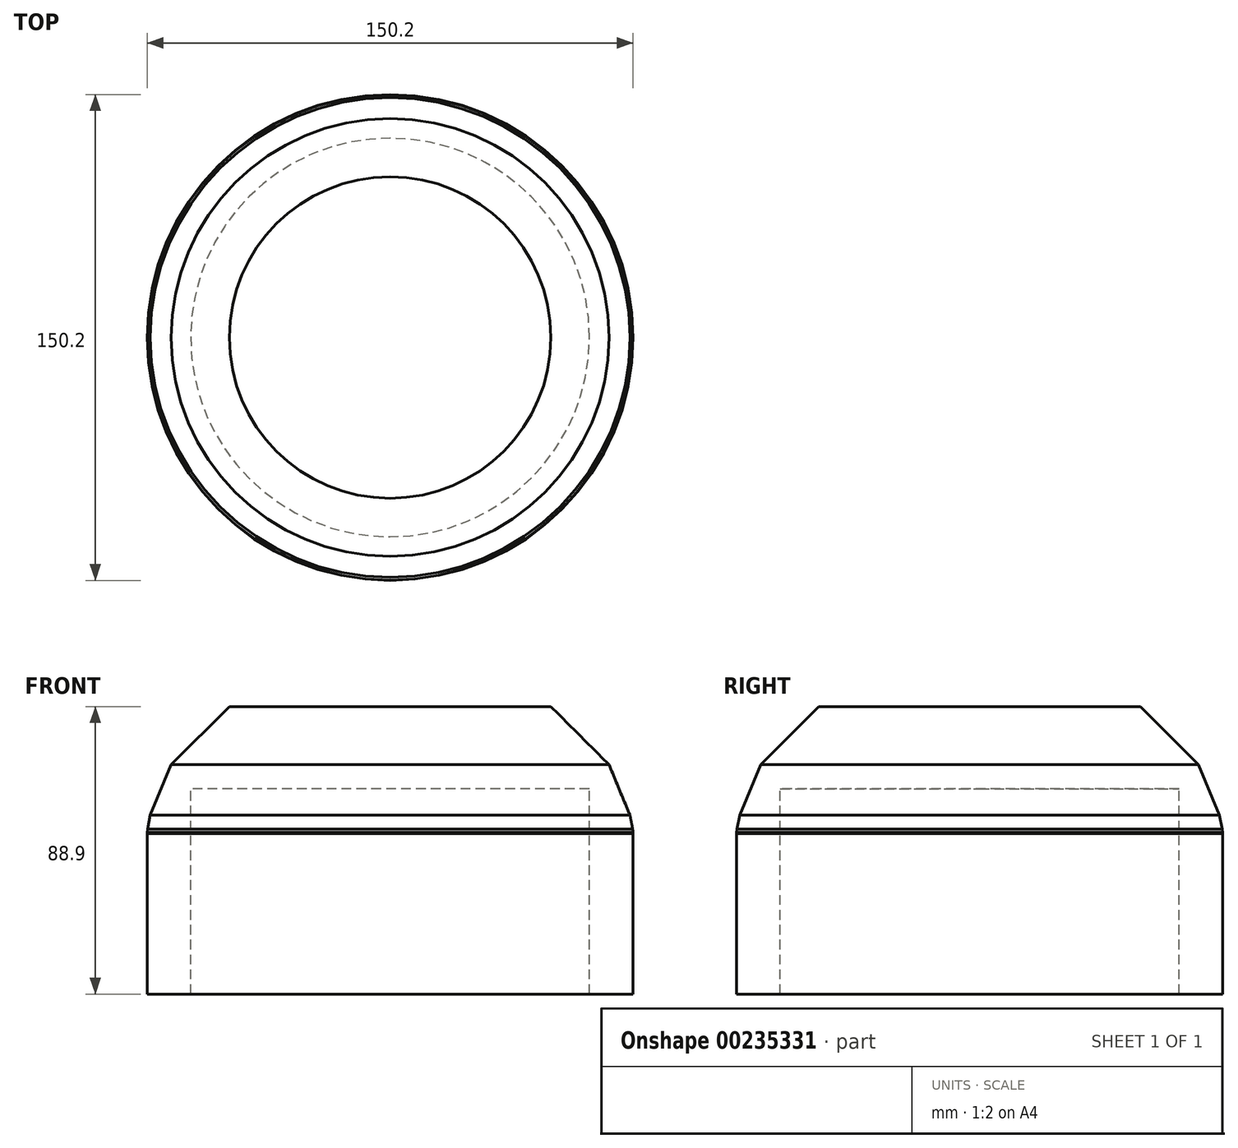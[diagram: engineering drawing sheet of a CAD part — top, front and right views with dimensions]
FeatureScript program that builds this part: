
annotation { "Feature Type Name" : "Feature", "Feature Type Description" : "" }
export const myFeature = defineFeature(function(context is Context, id is Id, definition is map)
    precondition{}
    {
        {
            var Q0;
            Q0=qCreatedBy(makeId("Top.planeOp"),FACE);
            var sketch = newSketch(context, id + "F0", { "sketchPlane" : qUnion([Q0])});
            skCircle(sketch, "E0", {"center": v(0, 0) * mm, "radius": 75.1 * mm});
            skSolve(sketch);
        }
        {
            var Q0;
            Q0=makeQuery(id+"F0.imprint","IMPRINT",FACE,{"disambiguationData":[TD([[makeQuery(id+"F0.imprint","IMPRINT",EDGE,{"derivedFrom":sQuery(id+"F0.wireOp",EDGE,"E0")}),1.0]])]});
            var sketch = newSketch(context, id + "F1", { "sketchPlane" : qUnion([Q0])});
            skCircle(sketch, "E1", {"center": v(0, 0) * mm, "radius": 61.62 * mm});
            skSolve(sketch);
        }
        {
            var Q0;
            Q0=makeQuery(id+"F1.imprint","IMPRINT",FACE,{"disambiguationData":[TD([[makeQuery(id+"F1.imprint","IMPRINT",EDGE,{"derivedFrom":sQuery(id+"F1.wireOp",EDGE,"E1")}),-1.0]])]});
            extrude(context, id + "F2", {"entities" : qUnion([Q0]), "oppositeDirection" : true, "depth" : 63.5 * mm});
        }
        {
            var Q0;
            Q0=makeQuery(id+"F0.imprint","IMPRINT",FACE,{"disambiguationData":[TD([[makeQuery(id+"F0.imprint","IMPRINT",EDGE,{"derivedFrom":sQuery(id+"F0.wireOp",EDGE,"E0")}),1.0]])]});
            extrude(context, id + "F7", {"entities" : qUnion([Q0]), "operationType" : NewBodyOperationType.ADD, "depth" : 25.4 * mm});
        }
        {
            var Q0;
            Q0=makeQuery(id+"F7.opExtrude","CAP_EDGE",EDGE,{"disambiguationData":[OSD([sQuery(id+"F0.wireOp",EDGE,"E0")])],"isStart":false});
            chamfer(context, id + "F8", {"entities" : qUnion([Q0]), "width" : 25.4 * mm, "tangentPropagation" : true});
        }
        {
            var Q0;
            {var subQ0=sQuery(id+"F0.wireOp",EDGE,"E0");Q0=makeQuery(id+"F8.opChamfer","BLEND_EDGE",EDGE,{"blendedFrom":[makeQuery(id+"F7.opExtrude","CAP_EDGE",EDGE,{"disambiguationData":[OSD([subQ0])],"isStart":false}),makeQuery(id+"F7.boolean.opBoolean","MERGE",FACE,{"derivedFrom":[makeQuery(id+"F2.opExtrude","SWEPT_FACE",FACE,{"disambiguationData":[OSD([subQ0])]}),makeQuery(id+"F7.opExtrude","SWEPT_FACE",FACE,{"disambiguationData":[OSD([subQ0])]})]})],"blendedInto":[makeQuery(id+"F7.boolean.opBoolean","MERGE",FACE,{"derivedFrom":[makeQuery(id+"F2.opExtrude","SWEPT_FACE",FACE,{"disambiguationData":[OSD([subQ0])]}),makeQuery(id+"F7.opExtrude","SWEPT_FACE",FACE,{"disambiguationData":[OSD([subQ0])]})]})]});}
            chamfer(context, id + "F3", {"entities" : qUnion([Q0]), "width" : 25.4 * mm, "tangentPropagation" : true});
        }
        {
            var Q0;
            {var subQ0=sQuery(id+"F0.wireOp",EDGE,"E0");var subQ1=makeQuery(id+"F7.boolean.opBoolean","MERGE",FACE,{"derivedFrom":[makeQuery(id+"F2.opExtrude","SWEPT_FACE",FACE,{"disambiguationData":[OSD([subQ0])]}),makeQuery(id+"F7.opExtrude","SWEPT_FACE",FACE,{"disambiguationData":[OSD([subQ0])]})]});Q0=makeQuery(id+"F3.opChamfer","BLEND_EDGE",EDGE,{"blendedFrom":[makeQuery(id+"F8.opChamfer","BLEND_EDGE",EDGE,{"blendedFrom":[makeQuery(id+"F7.opExtrude","CAP_EDGE",EDGE,{"disambiguationData":[OSD([subQ0])],"isStart":false}),subQ1],"blendedInto":[subQ1]}),subQ1],"blendedInto":[subQ1]});}
            chamfer(context, id + "F4", {"entities" : qUnion([Q0]), "width" : 12.7 * mm, "tangentPropagation" : true});
        }
        {
            var Q0;
            {var subQ0=sQuery(id+"F0.wireOp",EDGE,"E0");var subQ1=makeQuery(id+"F7.boolean.opBoolean","MERGE",FACE,{"derivedFrom":[makeQuery(id+"F2.opExtrude","SWEPT_FACE",FACE,{"disambiguationData":[OSD([subQ0])]}),makeQuery(id+"F7.opExtrude","SWEPT_FACE",FACE,{"disambiguationData":[OSD([subQ0])]})]});var subQ2=subQ1;Q0=makeQuery(id+"F4.opChamfer","BLEND_EDGE",EDGE,{"blendedFrom":[makeQuery(id+"F3.opChamfer","BLEND_EDGE",EDGE,{"blendedFrom":[makeQuery(id+"F8.opChamfer","BLEND_EDGE",EDGE,{"blendedFrom":[makeQuery(id+"F7.opExtrude","CAP_EDGE",EDGE,{"disambiguationData":[OSD([subQ0])],"isStart":false}),subQ1],"blendedInto":[subQ1]}),subQ2],"blendedInto":[subQ2]}),subQ2],"blendedInto":[subQ2]});}
            chamfer(context, id + "F9", {"entities" : qUnion([Q0]), "width" : 6.35 * mm, "tangentPropagation" : true});
        }
        {
            var Q0;
            {var subQ0=sQuery(id+"F0.wireOp",EDGE,"E0");var subQ1=makeQuery(id+"F7.boolean.opBoolean","MERGE",FACE,{"derivedFrom":[makeQuery(id+"F2.opExtrude","SWEPT_FACE",FACE,{"disambiguationData":[OSD([subQ0])]}),makeQuery(id+"F7.opExtrude","SWEPT_FACE",FACE,{"disambiguationData":[OSD([subQ0])]})]});var subQ2=subQ1;var subQ3=subQ2;Q0=makeQuery(id+"F9.opChamfer","BLEND_EDGE",EDGE,{"blendedFrom":[makeQuery(id+"F4.opChamfer","BLEND_EDGE",EDGE,{"blendedFrom":[makeQuery(id+"F3.opChamfer","BLEND_EDGE",EDGE,{"blendedFrom":[makeQuery(id+"F8.opChamfer","BLEND_EDGE",EDGE,{"blendedFrom":[makeQuery(id+"F7.opExtrude","CAP_EDGE",EDGE,{"disambiguationData":[OSD([subQ0])],"isStart":false}),subQ1],"blendedInto":[subQ1]}),subQ2],"blendedInto":[subQ2]}),subQ3],"blendedInto":[subQ3]}),subQ3],"blendedInto":[subQ3]});}
            chamfer(context, id + "F5", {"entities" : qUnion([Q0]), "width" : 3.17 * mm, "tangentPropagation" : true});
        }
    });
